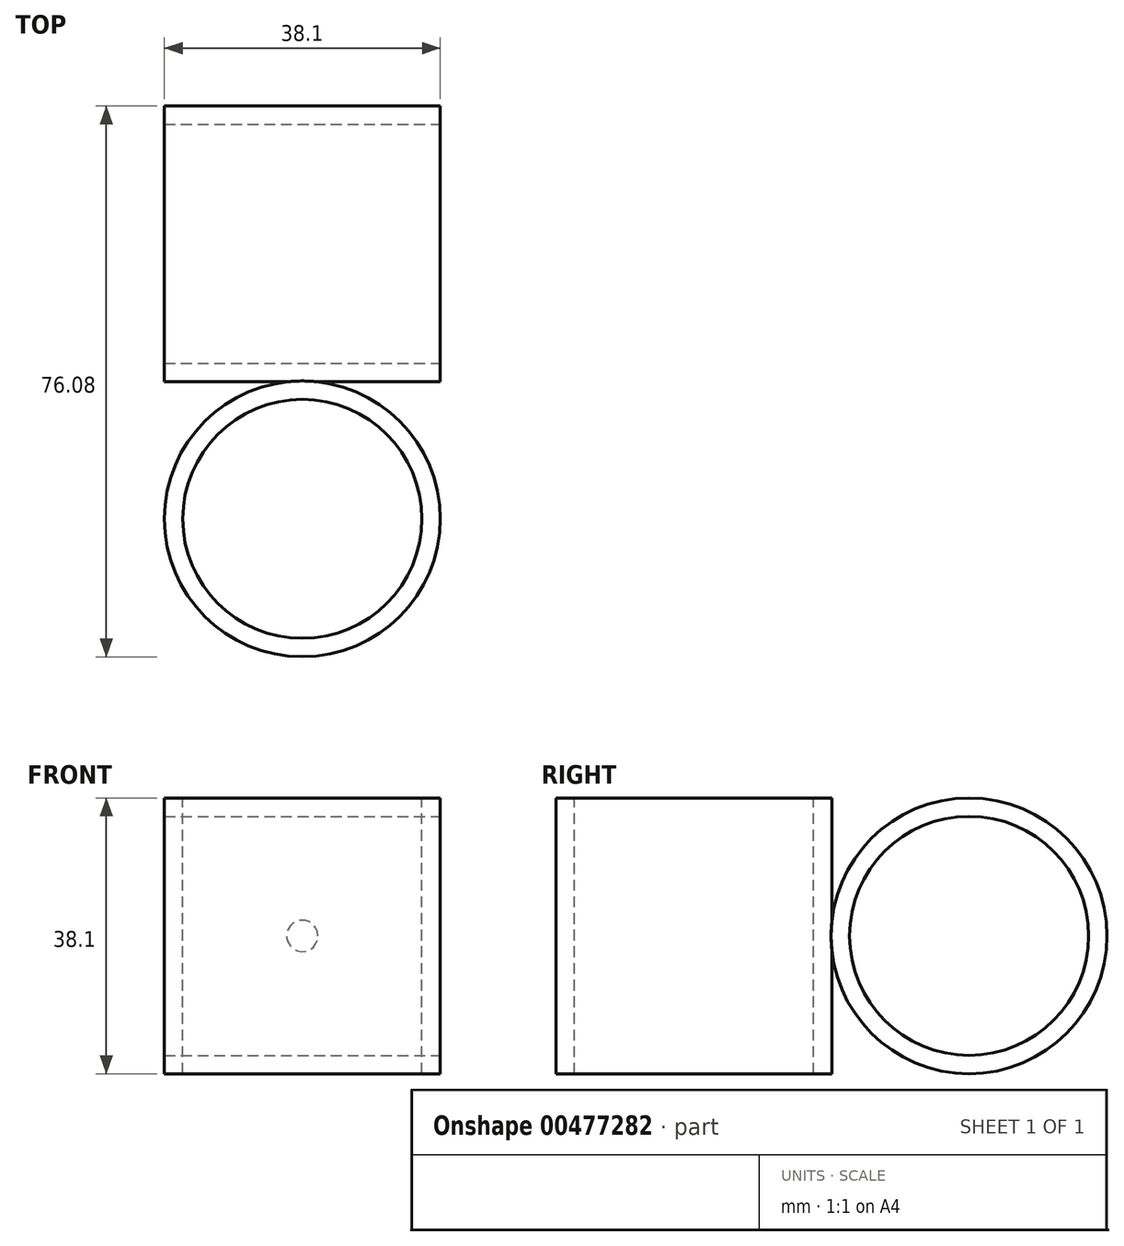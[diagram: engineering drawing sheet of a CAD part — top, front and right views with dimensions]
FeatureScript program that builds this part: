
annotation { "Feature Type Name" : "Feature", "Feature Type Description" : "" }
export const myFeature = defineFeature(function(context is Context, id is Id, definition is map)
    precondition{}
    {
        {
            var Q0;
            Q0=qCreatedBy(makeId("Front.planeOp"),FACE);
            var sketch = newSketch(context, id + "F0", { "sketchPlane" : qUnion([Q0])});
            skCircle(sketch, "E0", {"center": v(0, 0) * mm, "radius": 19.05 * mm});
            skSolve(sketch);
        }
        {
            var Q0;
            Q0=qCreatedBy(makeId("Right.planeOp"),FACE);
            var sketch = newSketch(context, id + "F1", { "sketchPlane" : qUnion([Q0])});
            skCircle(sketch, "E1", {"center": v(0, 0) * mm, "radius": 19.05 * mm});
            skSolve(sketch);
        }
        {
            var Q0;
            Q0=makeQuery(id+"F1.imprint","IMPRINT",FACE,{"disambiguationData":[TD([[makeQuery(id+"F1.imprint","IMPRINT",EDGE,{"derivedFrom":sQuery(id+"F1.wireOp",EDGE,"E1")}),1.0]])]});
            extrude(context, id + "F2", {"entities" : qUnion([Q0]), "endBound" : BoundingType.SYMMETRIC, "depth" : 38.1 * mm});
        }
        {
            var Q0;
            Q0=sQuery(id+"F1.wireOp",VERTEX,"E1.center");
            var Q1;
            Q1=makeQuery(id+"Fo3VGctr2HVEJEo_0.opExtrude","SWEPT_BODY",BODY,{"disambiguationData":[OSD([sQuery(id+"F0.wireOp",EDGE,"E0")])]});
            var Q2;
            Q2=makeQuery(id+"F2.opExtrude","SWEPT_BODY",BODY,{"disambiguationData":[OSD([sQuery(id+"F1.wireOp",EDGE,"E1")])]});
            hole(context, id + "F3", {"style" : HoleStyle.SIMPLE, "endStyle" : HoleEndStyle.THROUGH, "holeDiameter" : 33.02 * mm, "isTappedThrough" : true, "tappedDepth" : 12.7 * mm, "tapClearance" : 3, "startFromSketch" : true, "locations" : qUnion([Q0]), "scope" : qUnion([Q1, Q2])});
        }
        {
            var Q0;
            Q0=sQuery(id+"F1.wireOp",VERTEX,"E1.center");
            var Q1;
            Q1=makeQuery(id+"Fo3VGctr2HVEJEo_0.opExtrude","SWEPT_BODY",BODY,{"disambiguationData":[OSD([sQuery(id+"F0.wireOp",EDGE,"E0")])]});
            var Q2;
            Q2=makeQuery(id+"F2.opExtrude","SWEPT_BODY",BODY,{"disambiguationData":[OSD([sQuery(id+"F1.wireOp",EDGE,"E1")])]});
            hole(context, id + "F4", {"style" : HoleStyle.SIMPLE, "endStyle" : HoleEndStyle.THROUGH, "oppositeDirection" : true, "holeDiameter" : 33.02 * mm, "isTappedThrough" : true, "tappedDepth" : 12.7 * mm, "tapClearance" : 3, "startFromSketch" : true, "locations" : qUnion([Q0]), "scope" : qUnion([Q1, Q2])});
        }
        {
            var Q0;
            Q0=qCreatedBy(makeId("Top.planeOp"),FACE);
            var sketch = newSketch(context, id + "F5", { "sketchPlane" : qUnion([Q0])});
            skCircle(sketch, "E2", {"center": v(0, -37.98) * mm, "radius": 19.05 * mm});
            skSolve(sketch);
        }
        {
            var Q0;
            Q0=makeQuery(id+"F5.imprint","IMPRINT",FACE,{"disambiguationData":[TD([[makeQuery(id+"F5.imprint","IMPRINT",EDGE,{"derivedFrom":sQuery(id+"F5.wireOp",EDGE,"E2")}),1.0]])]});
            extrude(context, id + "F6", {"entities" : qUnion([Q0]), "operationType" : NewBodyOperationType.ADD, "endBound" : BoundingType.SYMMETRIC, "depth" : 38.1 * mm});
        }
        {
            var Q0;
            Q0=sQuery(id+"F5.wireOp",VERTEX,"E2.center");
            var Q1;
            Q1=makeQuery(id+"F2.opExtrude","SWEPT_BODY",BODY,{"disambiguationData":[OSD([sQuery(id+"F1.wireOp",EDGE,"E1")])]});
            hole(context, id + "F7", {"style" : HoleStyle.SIMPLE, "endStyle" : HoleEndStyle.THROUGH, "holeDiameter" : 33.02 * mm, "isTappedThrough" : true, "tappedDepth" : 12.7 * mm, "tapClearance" : 3, "locations" : qUnion([Q0]), "scope" : qUnion([Q1])});
        }
        {
            var Q0;
            Q0=sQuery(id+"F5.wireOp",VERTEX,"E2.center");
            var Q1;
            Q1=makeQuery(id+"F2.opExtrude","SWEPT_BODY",BODY,{"disambiguationData":[OSD([sQuery(id+"F1.wireOp",EDGE,"E1")])]});
            hole(context, id + "F8", {"style" : HoleStyle.SIMPLE, "endStyle" : HoleEndStyle.THROUGH, "oppositeDirection" : true, "holeDiameter" : 33.02 * mm, "isTappedThrough" : true, "tappedDepth" : 12.7 * mm, "tapClearance" : 3, "locations" : qUnion([Q0]), "scope" : qUnion([Q1])});
        }
    });
